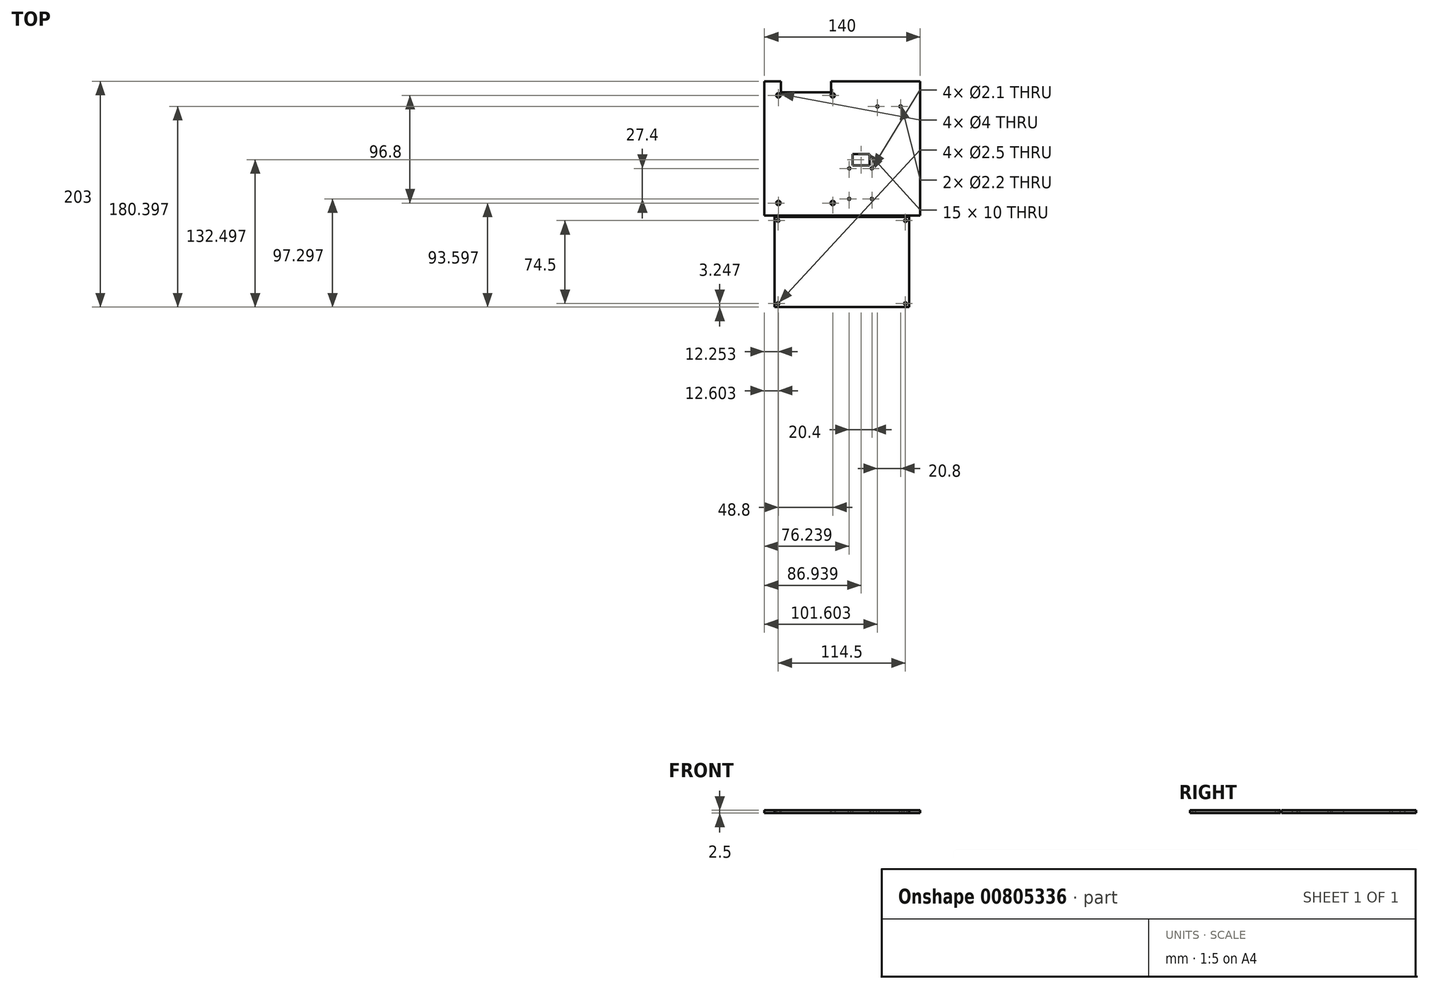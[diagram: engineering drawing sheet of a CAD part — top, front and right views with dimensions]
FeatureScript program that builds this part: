
annotation { "Feature Type Name" : "Feature", "Feature Type Description" : "" }
export const myFeature = defineFeature(function(context is Context, id is Id, definition is map)
    precondition{}
    {
        {
            var Q0;
            Q0=qCreatedBy(makeId("Top.planeOp"),FACE);
            var sketch = newSketch(context, id + "F0", { "sketchPlane" : qUnion([Q0])});
            skLineSegment(sketch, "E0.bottom", {"start": v(-96.6, 98.7) * mm, "end": v(43.4, 98.7) * mm});
            skLineSegment(sketch, "E0.top", {"start": v(-96.6, -126.3) * mm, "end": v(43.4, -126.3) * mm});
            skLineSegment(sketch, "E0.left", {"start": v(-96.6, 98.7) * mm, "end": v(-96.6, -126.3) * mm});
            skLineSegment(sketch, "E0.right", {"start": v(43.4, 98.7) * mm, "end": v(43.4, -126.3) * mm});
            skLineSegment(sketch, "E1.bottom", {"start": v(-86.6, 88.7) * mm, "end": v(-32.6, 88.7) * mm});
            skLineSegment(sketch, "E1.top", {"start": v(-86.6, -13.3) * mm, "end": v(-32.6, -13.3) * mm});
            skLineSegment(sketch, "E1.left", {"start": v(-86.6, 88.7) * mm, "end": v(-86.6, -13.3) * mm});
            skLineSegment(sketch, "E1.right", {"start": v(-32.6, 88.7) * mm, "end": v(-32.6, -13.3) * mm});
            skLineSegment(sketch, "E2.bottom", {"start": v(-87.6, -23.3) * mm, "end": v(33.4, -23.3) * mm});
            skLineSegment(sketch, "E2.top", {"start": v(-87.6, -104.3) * mm, "end": v(33.4, -104.3) * mm});
            skLineSegment(sketch, "E2.left", {"start": v(-87.6, -23.3) * mm, "end": v(-87.6, -104.3) * mm});
            skLineSegment(sketch, "E2.right", {"start": v(33.4, -23.3) * mm, "end": v(33.4, -104.3) * mm});
            skLineSegment(sketch, "E3.bottom", {"start": v(-23.16, 23.2) * mm, "end": v(2.84, 23.2) * mm});
            skLineSegment(sketch, "E3.top", {"start": v(-23.16, -9.8) * mm, "end": v(2.84, -9.8) * mm});
            skLineSegment(sketch, "E3.left", {"start": v(-23.16, 23.2) * mm, "end": v(-23.16, -9.8) * mm});
            skLineSegment(sketch, "E3.right", {"start": v(2.84, 23.2) * mm, "end": v(2.84, -9.8) * mm});
            skLineSegment(sketch, "E4.bottom", {"start": v(2.4, 78.7) * mm, "end": v(28.4, 78.7) * mm});
            skLineSegment(sketch, "E4.top", {"start": v(2.4, 43.2) * mm, "end": v(28.4, 43.2) * mm});
            skLineSegment(sketch, "E4.left", {"start": v(2.4, 78.7) * mm, "end": v(2.4, 43.2) * mm});
            skLineSegment(sketch, "E4.right", {"start": v(28.4, 78.7) * mm, "end": v(28.4, 43.2) * mm});
            skLineSegment(sketch, "E5", {"start": v(2.84, 23.2) * mm, "end": v(-2.16, 23.2) * mm});
            skLineSegment(sketch, "E6", {"start": v(-2.16, 23.2) * mm, "end": v(-17.16, 23.2) * mm});
            skLineSegment(sketch, "E7", {"start": v(-2.16, 23.2) * mm, "end": v(-2.16, 33.2) * mm});
            skLineSegment(sketch, "E8.bottom", {"start": v(-17.16, 23.2) * mm, "end": v(-2.16, 23.2) * mm});
            skLineSegment(sketch, "E8.top", {"start": v(-17.16, 33.2) * mm, "end": v(-2.16, 33.2) * mm});
            skLineSegment(sketch, "E8.left", {"start": v(-17.16, 23.2) * mm, "end": v(-17.16, 33.2) * mm});
            skLineSegment(sketch, "E9.bottom", {"start": v(-81.6, 98.7) * mm, "end": v(-36.6, 98.7) * mm});
            skLineSegment(sketch, "E9.top", {"start": v(-81.6, 88.7) * mm, "end": v(-36.6, 88.7) * mm});
            skLineSegment(sketch, "E9.left", {"start": v(-81.6, 98.7) * mm, "end": v(-81.6, 88.7) * mm});
            skLineSegment(sketch, "E9.right", {"start": v(-36.6, 98.7) * mm, "end": v(-36.6, 88.7) * mm});
            skLineSegment(sketch, "E10", {"start": v(33.4, -23.3) * mm, "end": v(33.4, -43.3) * mm});
            skLineSegment(sketch, "E11.bottom", {"start": v(33.4, -43.3) * mm, "end": v(43.4, -43.3) * mm});
            skLineSegment(sketch, "E11.top", {"start": v(33.4, -23.3) * mm, "end": v(43.4, -23.3) * mm});
            skLineSegment(sketch, "E11.left", {"start": v(33.4, -43.3) * mm, "end": v(33.4, -23.3) * mm});
            skLineSegment(sketch, "E11.right", {"start": v(43.4, -43.3) * mm, "end": v(43.4, -23.3) * mm});
            skCircle(sketch, "E12", {"center": v(-84.35, -101.04) * mm, "radius": 1.25 * mm});
            skCircle(sketch, "E13", {"center": v(-84.35, -26.54) * mm, "radius": 1.25 * mm});
            skCircle(sketch, "E14", {"center": v(30.15, -26.54) * mm, "radius": 1.25 * mm});
            skCircle(sketch, "E15", {"center": v(30.15, -101.04) * mm, "radius": 1.25 * mm});
            skCircle(sketch, "E16", {"center": v(5, 76.1) * mm, "radius": 1.1 * mm});
            skCircle(sketch, "E17", {"center": v(25.8, 76.1) * mm, "radius": 1.1 * mm});
            skCircle(sketch, "E18", {"center": v(0.04, 20.4) * mm, "radius": 1.05 * mm});
            skCircle(sketch, "E19", {"center": v(0.04, -7) * mm, "radius": 1.05 * mm});
            skCircle(sketch, "E20", {"center": v(-20.36, -7) * mm, "radius": 1.05 * mm});
            skCircle(sketch, "E21", {"center": v(-20.36, 20.4) * mm, "radius": 1.05 * mm});
            skLineSegment(sketch, "E22.bottom", {"start": v(-86.6, 88.7) * mm, "end": v(-84.4, 88.7) * mm});
            skLineSegment(sketch, "E22.left", {"start": v(-86.6, 88.7) * mm, "end": v(-86.6, 86.5) * mm});
            skLineSegment(sketch, "E23.bottom", {"start": v(-86.6, 88.7) * mm, "end": v(-84, 88.7) * mm});
            skLineSegment(sketch, "E23.left", {"start": v(-86.6, 88.7) * mm, "end": v(-86.6, 86.1) * mm});
            skCircle(sketch, "E24", {"center": v(-84, 86.1) * mm, "radius": 2 * mm});
            skLineSegment(sketch, "E25.bottom", {"start": v(-32.6, 88.7) * mm, "end": v(-35.2, 88.7) * mm});
            skLineSegment(sketch, "E25.left", {"start": v(-32.6, 88.7) * mm, "end": v(-32.6, 86.1) * mm});
            skCircle(sketch, "E26", {"center": v(-35.2, 86.1) * mm, "radius": 2 * mm});
            skLineSegment(sketch, "E27.bottom", {"start": v(-32.6, -13.3) * mm, "end": v(-35.2, -13.3) * mm});
            skLineSegment(sketch, "E27.left", {"start": v(-32.6, -13.3) * mm, "end": v(-32.6, -10.7) * mm});
            skLineSegment(sketch, "E28.bottom", {"start": v(-86.6, -13.3) * mm, "end": v(-84, -13.3) * mm});
            skLineSegment(sketch, "E28.left", {"start": v(-86.6, -13.3) * mm, "end": v(-86.6, -10.7) * mm});
            skCircle(sketch, "E29", {"center": v(-84, -10.7) * mm, "radius": 2 * mm});
            skCircle(sketch, "E30", {"center": v(-35.2, -10.7) * mm, "radius": 2 * mm});
            skLineSegment(sketch, "E31.bottom", {"start": v(43.4, -23.3) * mm, "end": v(-96.6, -23.3) * mm});
            skLineSegment(sketch, "E31.top", {"start": v(43.4, -22.07) * mm, "end": v(-96.6, -22.07) * mm});
            skLineSegment(sketch, "E31.left", {"start": v(43.4, -23.3) * mm, "end": v(43.4, -22.07) * mm});
            skLineSegment(sketch, "E31.right", {"start": v(-96.6, -23.3) * mm, "end": v(-96.6, -22.07) * mm});
            skSolve(sketch);
        }
        {
            var Q0;
            Q0=makeQuery(id+"F0.imprint","IMPRINT",FACE,{"disambiguationData":[TD([[makeQuery(id+"F0.imprint","IMPRINT",EDGE,{"derivedFrom":sQuery(id+"F0.wireOp",EDGE,"E2.bottom")}),-1.0]])]});
            var Q1;
            Q1=makeQuery(id+"F0.imprint","IMPRINT",FACE,{"disambiguationData":[TD([[makeQuery(id+"F0.imprint","IMPRINT",EDGE,{"derivedFrom":sQuery(id+"F0.wireOp",EDGE,"E1.top")}),1.0]])]});
            var Q2;
            Q2=makeQuery(id+"F0.imprint","IMPRINT",FACE,{"disambiguationData":[TD([[makeQuery(id+"F0.imprint","IMPRINT",EDGE,{"derivedFrom":sQuery(id+"F0.wireOp",EDGE,"E3.bottom")}),-1.0]])]});
            var Q3;
            Q3=makeQuery(id+"F0.imprint","IMPRINT",FACE,{"disambiguationData":[TD([[makeQuery(id+"F0.imprint","IMPRINT",EDGE,{"derivedFrom":sQuery(id+"F0.wireOp",EDGE,"E8.bottom")}),1.0]])]});
            var Q4;
            Q4=makeQuery(id+"F0.imprint","IMPRINT",FACE,{"disambiguationData":[TD([[makeQuery(id+"F0.imprint","IMPRINT",EDGE,{"derivedFrom":sQuery(id+"F0.wireOp",EDGE,"E4.bottom")}),-1.0]])]});
            var Q5;
            Q5=makeQuery(id+"F0.imprint","IMPRINT",FACE,{"disambiguationData":[TD([[makeQuery(id+"F0.imprint","IMPRINT",EDGE,{"derivedFrom":sQuery(id+"F0.wireOp",EDGE,"E9.bottom")}),-1.0]])]});
            var Q6;
            Q6=makeQuery(id+"F0.imprint","IMPRINT",FACE,{"disambiguationData":[TD([[makeQuery(id+"F0.imprint","IMPRINT",EDGE,{"derivedFrom":sQuery(id+"F0.wireOp",EDGE,"E1.top")}),-1.0]])]});
            extrude(context, id + "F1", {"entities" : qUnion([Q0, Q1, Q2, Q3, Q4, Q5, Q6]), "depth" : 2.5 * mm, "offsetDistance" : 25 * mm});
        }
    });
